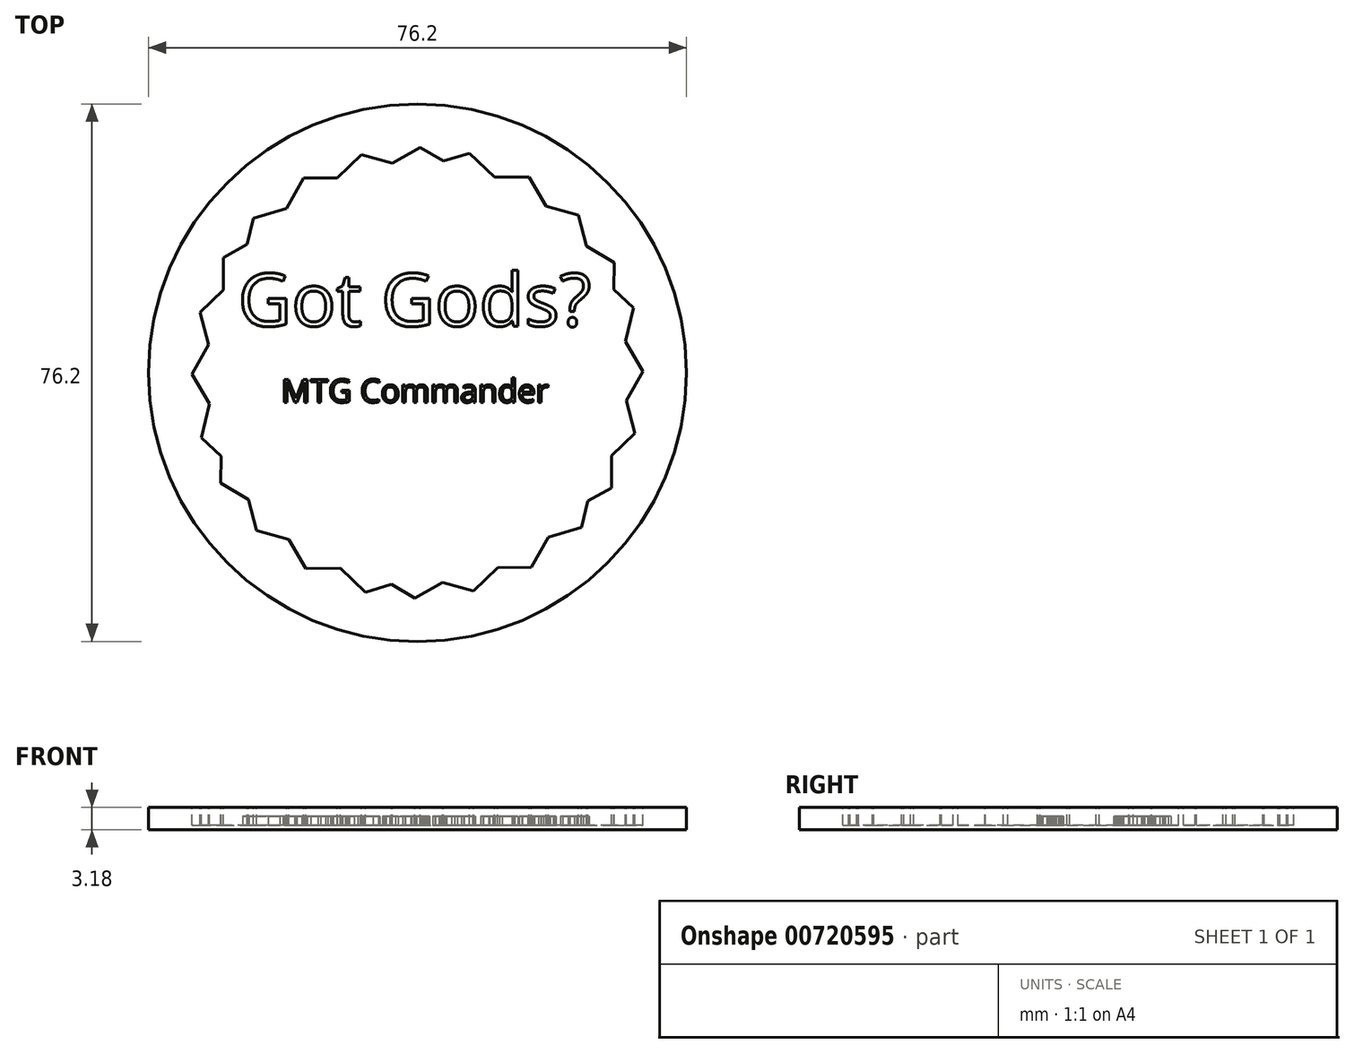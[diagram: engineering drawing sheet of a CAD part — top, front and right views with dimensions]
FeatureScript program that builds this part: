
annotation { "Feature Type Name" : "Feature", "Feature Type Description" : "" }
export const myFeature = defineFeature(function(context is Context, id is Id, definition is map)
    precondition{}
    {
        {
            var Q0;
            Q0=qCreatedBy(makeId("Top.planeOp"),FACE);
            var sketch = newSketch(context, id + "F0", { "sketchPlane" : qUnion([Q0])});
            skCircle(sketch, "E0", {"center": v(0, 0) * mm, "radius": 38.1 * mm});
            skSolve(sketch);
        }
        {
            var Q0;
            Q0=makeQuery(id+"F0.imprint","IMPRINT",FACE,{"disambiguationData":[TD([[makeQuery(id+"F0.imprint","IMPRINT",EDGE,{"derivedFrom":sQuery(id+"F0.wireOp",EDGE,"E0")}),1.0]])]});
            extrude(context, id + "F1", {"entities" : qUnion([Q0]), "depth" : 3.17 * mm, "offsetDistance" : 25.4 * mm});
        }
        {
            var Q0;
            Q0=makeQuery(id+"F1.opExtrude","CAP_FACE",FACE,{"disambiguationData":[OSD([sQuery(id+"F0.wireOp",EDGE,"E0")])],"isStart":false});
            var sketch = newSketch(context, id + "F2", { "sketchPlane" : qUnion([Q0])});
            skCircle(sketch, "E1", {"center": v(0, 0) * mm, "radius": 34.93 * mm});
            skCircle(sketch, "E2.cCircle", {"center": v(0, 0) * mm, "radius": 27.67 * mm, "construction": true});
            skLineSegment(sketch, "E2.0", {"start": v(15.83, 27.75) * mm, "end": v(31.95, 0.17) * mm});
            skLineSegment(sketch, "E2.1", {"start": v(31.95, 0.17) * mm, "end": v(16.12, -27.58) * mm});
            skLineSegment(sketch, "E2.2", {"start": v(16.12, -27.58) * mm, "end": v(-15.83, -27.75) * mm});
            skLineSegment(sketch, "E2.3", {"start": v(-15.83, -27.75) * mm, "end": v(-31.95, -0.17) * mm});
            skLineSegment(sketch, "E2.4", {"start": v(-31.95, -0.17) * mm, "end": v(-16.12, 27.58) * mm});
            skLineSegment(sketch, "E2.5", {"start": v(-16.12, 27.58) * mm, "end": v(15.83, 27.75) * mm});
            skPoint(sketch, "E2.0.midPoint", {"position": v(23.89, 13.96) * mm});
            skLineSegment(sketch, "E3.0", {"start": v(0.4, 31.95) * mm, "end": v(27.87, 15.63) * mm});
            skLineSegment(sketch, "E3.1", {"start": v(27.87, 15.63) * mm, "end": v(27.47, -16.32) * mm});
            skLineSegment(sketch, "E3.2", {"start": v(27.47, -16.32) * mm, "end": v(-0.4, -31.95) * mm});
            skLineSegment(sketch, "E3.3", {"start": v(-0.4, -31.95) * mm, "end": v(-27.87, -15.63) * mm});
            skLineSegment(sketch, "E3.4", {"start": v(-27.87, -15.63) * mm, "end": v(-27.47, 16.32) * mm});
            skLineSegment(sketch, "E3.5", {"start": v(-27.47, 16.32) * mm, "end": v(0.4, 31.95) * mm});
            skPoint(sketch, "E3.0.midPoint", {"position": v(14.13, 23.79) * mm});
            skLineSegment(sketch, "E4.0", {"start": v(22.82, 22.36) * mm, "end": v(30.78, -8.58) * mm});
            skLineSegment(sketch, "E4.1", {"start": v(30.78, -8.58) * mm, "end": v(7.96, -30.94) * mm});
            skLineSegment(sketch, "E4.2", {"start": v(7.96, -30.94) * mm, "end": v(-22.82, -22.36) * mm});
            skLineSegment(sketch, "E4.3", {"start": v(-22.82, -22.36) * mm, "end": v(-30.78, 8.58) * mm});
            skLineSegment(sketch, "E4.4", {"start": v(-30.78, 8.58) * mm, "end": v(-7.96, 30.94) * mm});
            skLineSegment(sketch, "E4.5", {"start": v(-7.96, 30.94) * mm, "end": v(22.82, 22.36) * mm});
            skPoint(sketch, "E4.0.midPoint", {"position": v(26.8, 6.9) * mm});
            skLineSegment(sketch, "E5.0", {"start": v(-23.26, 21.9) * mm, "end": v(7.34, 31.1) * mm});
            skLineSegment(sketch, "E5.1", {"start": v(7.34, 31.1) * mm, "end": v(30.6, 9.19) * mm});
            skLineSegment(sketch, "E5.2", {"start": v(30.6, 9.19) * mm, "end": v(23.26, -21.9) * mm});
            skLineSegment(sketch, "E5.3", {"start": v(23.26, -21.9) * mm, "end": v(-7.34, -31.1) * mm});
            skLineSegment(sketch, "E5.4", {"start": v(-7.34, -31.1) * mm, "end": v(-30.6, -9.19) * mm});
            skLineSegment(sketch, "E5.5", {"start": v(-30.6, -9.19) * mm, "end": v(-23.26, 21.9) * mm});
            skPoint(sketch, "E5.0.midPoint", {"position": v(-7.96, 26.5) * mm});
            skSolve(sketch);
        }
        {
            var Q0;
            {var subQ0=sQuery(id+"F2.wireOp",EDGE,"E4.2");var subQ1=sQuery(id+"F2.wireOp",EDGE,"E2.3");var subQ2=makeQuery(id+"F2.imprint","INTERSECT",VERTEX,{"derivedFrom":[subQ1,subQ0]});Q0=makeQuery(id+"F2.imprint","IMPRINT",FACE,{"disambiguationData":[TD([[makeQuery(id+"F2.imprint","IMPRINT",EDGE,{"disambiguationData":[TD([[subQ2,-1.0]])],"derivedFrom":subQ1}),-1.0]])]});}
            var Q1;
            {var subQ0=sQuery(id+"F2.wireOp",EDGE,"E2.3");var subQ1=sQuery(id+"F2.wireOp",EDGE,"E2.2");var subQ2=makeQuery(id+"F2.imprint","INTERSECT",VERTEX,{"derivedFrom":[subQ1,subQ0]});Q1=makeQuery(id+"F2.imprint","IMPRINT",FACE,{"disambiguationData":[TD([[makeQuery(id+"F2.imprint","IMPRINT",EDGE,{"disambiguationData":[TD([[subQ2,1.0]])],"derivedFrom":subQ1}),-1.0]])]});}
            var Q2;
            {var subQ0=sQuery(id+"F2.wireOp",EDGE,"E4.2");var subQ1=sQuery(id+"F2.wireOp",EDGE,"E2.2");var subQ2=makeQuery(id+"F2.imprint","INTERSECT",VERTEX,{"derivedFrom":[subQ1,subQ0]});Q2=makeQuery(id+"F2.imprint","IMPRINT",FACE,{"disambiguationData":[TD([[makeQuery(id+"F2.imprint","IMPRINT",EDGE,{"disambiguationData":[TD([[subQ2,-1.0]])],"derivedFrom":subQ1}),-1.0]])]});}
            var Q3;
            {var subQ0=sQuery(id+"F2.wireOp",EDGE,"E4.2");var subQ1=sQuery(id+"F2.wireOp",EDGE,"E2.2");var subQ2=makeQuery(id+"F2.imprint","INTERSECT",VERTEX,{"derivedFrom":[subQ1,subQ0]});Q3=makeQuery(id+"F2.imprint","IMPRINT",FACE,{"disambiguationData":[TD([[makeQuery(id+"F2.imprint","IMPRINT",EDGE,{"disambiguationData":[TD([[subQ2,-1.0]])],"derivedFrom":subQ1}),1.0]])]});}
            var Q4;
            {var subQ0=sQuery(id+"F2.wireOp",EDGE,"E3.2");var subQ1=sQuery(id+"F2.wireOp",EDGE,"E2.2");var subQ2=makeQuery(id+"F2.imprint","INTERSECT",VERTEX,{"derivedFrom":[subQ1,subQ0]});Q4=makeQuery(id+"F2.imprint","IMPRINT",FACE,{"disambiguationData":[TD([[makeQuery(id+"F2.imprint","IMPRINT",EDGE,{"disambiguationData":[TD([[subQ2,-1.0]])],"derivedFrom":subQ1}),1.0]])]});}
            var Q5;
            {var subQ0=sQuery(id+"F2.wireOp",EDGE,"E4.1");var subQ1=sQuery(id+"F2.wireOp",EDGE,"E2.2");var subQ2=makeQuery(id+"F2.imprint","INTERSECT",VERTEX,{"derivedFrom":[subQ1,subQ0]});Q5=makeQuery(id+"F2.imprint","IMPRINT",FACE,{"disambiguationData":[TD([[makeQuery(id+"F2.imprint","IMPRINT",EDGE,{"disambiguationData":[TD([[subQ2,-1.0]])],"derivedFrom":subQ1}),1.0]])]});}
            var Q6;
            {var subQ0=sQuery(id+"F2.wireOp",EDGE,"E4.1");var subQ1=sQuery(id+"F2.wireOp",EDGE,"E2.2");var subQ2=makeQuery(id+"F2.imprint","INTERSECT",VERTEX,{"derivedFrom":[subQ1,subQ0]});Q6=makeQuery(id+"F2.imprint","IMPRINT",FACE,{"disambiguationData":[TD([[makeQuery(id+"F2.imprint","IMPRINT",EDGE,{"disambiguationData":[TD([[subQ2,-1.0]])],"derivedFrom":subQ1}),-1.0]])]});}
            var Q7;
            {var subQ0=sQuery(id+"F2.wireOp",EDGE,"E2.2");var subQ1=sQuery(id+"F2.wireOp",EDGE,"E2.1");var subQ2=makeQuery(id+"F2.imprint","INTERSECT",VERTEX,{"derivedFrom":[subQ1,subQ0]});Q7=makeQuery(id+"F2.imprint","IMPRINT",FACE,{"disambiguationData":[TD([[makeQuery(id+"F2.imprint","IMPRINT",EDGE,{"disambiguationData":[TD([[subQ2,1.0]])],"derivedFrom":subQ1}),-1.0]])]});}
            var Q8;
            {var subQ15=sQuery(id+"F2.wireOp",EDGE,"E3.0");var subQ16=sQuery(id+"F2.wireOp",EDGE,"E2.0");var subQ17=makeQuery(id+"F2.imprint","INTERSECT",VERTEX,{"derivedFrom":[subQ16,subQ15]});Q8=makeQuery(id+"F2.imprint","IMPRINT",FACE,{"disambiguationData":[TD([[makeQuery(id+"F2.imprint","IMPRINT",EDGE,{"disambiguationData":[TD([[subQ17,-1.0]])],"derivedFrom":subQ16}),-1.0]])]});}
            var Q9;
            {var subQ0=sQuery(id+"F2.wireOp",EDGE,"E4.1");var subQ1=sQuery(id+"F2.wireOp",EDGE,"E2.1");var subQ2=makeQuery(id+"F2.imprint","INTERSECT",VERTEX,{"derivedFrom":[subQ1,subQ0]});Q9=makeQuery(id+"F2.imprint","IMPRINT",FACE,{"disambiguationData":[TD([[makeQuery(id+"F2.imprint","IMPRINT",EDGE,{"disambiguationData":[TD([[subQ2,-1.0]])],"derivedFrom":subQ1}),-1.0]])]});}
            var Q10;
            {var subQ0=sQuery(id+"F2.wireOp",EDGE,"E4.1");var subQ1=sQuery(id+"F2.wireOp",EDGE,"E2.1");var subQ2=makeQuery(id+"F2.imprint","INTERSECT",VERTEX,{"derivedFrom":[subQ1,subQ0]});Q10=makeQuery(id+"F2.imprint","IMPRINT",FACE,{"disambiguationData":[TD([[makeQuery(id+"F2.imprint","IMPRINT",EDGE,{"disambiguationData":[TD([[subQ2,-1.0]])],"derivedFrom":subQ1}),1.0]])]});}
            var Q11;
            {var subQ0=sQuery(id+"F2.wireOp",EDGE,"E3.1");var subQ1=sQuery(id+"F2.wireOp",EDGE,"E2.1");var subQ2=makeQuery(id+"F2.imprint","INTERSECT",VERTEX,{"derivedFrom":[subQ1,subQ0]});Q11=makeQuery(id+"F2.imprint","IMPRINT",FACE,{"disambiguationData":[TD([[makeQuery(id+"F2.imprint","IMPRINT",EDGE,{"disambiguationData":[TD([[subQ2,-1.0]])],"derivedFrom":subQ1}),1.0]])]});}
            var Q12;
            {var subQ0=sQuery(id+"F2.wireOp",EDGE,"E4.0");var subQ1=sQuery(id+"F2.wireOp",EDGE,"E2.1");var subQ2=makeQuery(id+"F2.imprint","INTERSECT",VERTEX,{"derivedFrom":[subQ1,subQ0]});Q12=makeQuery(id+"F2.imprint","IMPRINT",FACE,{"disambiguationData":[TD([[makeQuery(id+"F2.imprint","IMPRINT",EDGE,{"disambiguationData":[TD([[subQ2,-1.0]])],"derivedFrom":subQ1}),1.0]])]});}
            var Q13;
            {var subQ0=sQuery(id+"F2.wireOp",EDGE,"E4.0");var subQ1=sQuery(id+"F2.wireOp",EDGE,"E2.1");var subQ2=makeQuery(id+"F2.imprint","INTERSECT",VERTEX,{"derivedFrom":[subQ1,subQ0]});Q13=makeQuery(id+"F2.imprint","IMPRINT",FACE,{"disambiguationData":[TD([[makeQuery(id+"F2.imprint","IMPRINT",EDGE,{"disambiguationData":[TD([[subQ2,-1.0]])],"derivedFrom":subQ1}),-1.0]])]});}
            var Q14;
            {var subQ0=sQuery(id+"F2.wireOp",EDGE,"E2.1");var subQ1=sQuery(id+"F2.wireOp",EDGE,"E2.0");var subQ2=makeQuery(id+"F2.imprint","INTERSECT",VERTEX,{"derivedFrom":[subQ1,subQ0]});Q14=makeQuery(id+"F2.imprint","IMPRINT",FACE,{"disambiguationData":[TD([[makeQuery(id+"F2.imprint","IMPRINT",EDGE,{"disambiguationData":[TD([[subQ2,1.0]])],"derivedFrom":subQ1}),-1.0]])]});}
            var Q15;
            {var subQ0=sQuery(id+"F2.wireOp",EDGE,"E4.0");var subQ1=sQuery(id+"F2.wireOp",EDGE,"E2.0");var subQ2=makeQuery(id+"F2.imprint","INTERSECT",VERTEX,{"derivedFrom":[subQ1,subQ0]});Q15=makeQuery(id+"F2.imprint","IMPRINT",FACE,{"disambiguationData":[TD([[makeQuery(id+"F2.imprint","IMPRINT",EDGE,{"disambiguationData":[TD([[subQ2,-1.0]])],"derivedFrom":subQ1}),-1.0]])]});}
            var Q16;
            {var subQ0=sQuery(id+"F2.wireOp",EDGE,"E4.0");var subQ1=sQuery(id+"F2.wireOp",EDGE,"E2.0");var subQ2=makeQuery(id+"F2.imprint","INTERSECT",VERTEX,{"derivedFrom":[subQ1,subQ0]});Q16=makeQuery(id+"F2.imprint","IMPRINT",FACE,{"disambiguationData":[TD([[makeQuery(id+"F2.imprint","IMPRINT",EDGE,{"disambiguationData":[TD([[subQ2,-1.0]])],"derivedFrom":subQ1}),1.0]])]});}
            var Q17;
            {var subQ0=sQuery(id+"F2.wireOp",EDGE,"E3.0");var subQ1=sQuery(id+"F2.wireOp",EDGE,"E2.0");var subQ2=makeQuery(id+"F2.imprint","INTERSECT",VERTEX,{"derivedFrom":[subQ1,subQ0]});Q17=makeQuery(id+"F2.imprint","IMPRINT",FACE,{"disambiguationData":[TD([[makeQuery(id+"F2.imprint","IMPRINT",EDGE,{"disambiguationData":[TD([[subQ2,-1.0]])],"derivedFrom":subQ1}),1.0]])]});}
            var Q18;
            {var subQ0=sQuery(id+"F2.wireOp",EDGE,"E4.5");var subQ1=sQuery(id+"F2.wireOp",EDGE,"E2.0");var subQ2=makeQuery(id+"F2.imprint","INTERSECT",VERTEX,{"derivedFrom":[subQ1,subQ0]});Q18=makeQuery(id+"F2.imprint","IMPRINT",FACE,{"disambiguationData":[TD([[makeQuery(id+"F2.imprint","IMPRINT",EDGE,{"disambiguationData":[TD([[subQ2,-1.0]])],"derivedFrom":subQ1}),1.0]])]});}
            var Q19;
            {var subQ0=sQuery(id+"F2.wireOp",EDGE,"E4.5");var subQ1=sQuery(id+"F2.wireOp",EDGE,"E2.0");var subQ2=makeQuery(id+"F2.imprint","INTERSECT",VERTEX,{"derivedFrom":[subQ1,subQ0]});Q19=makeQuery(id+"F2.imprint","IMPRINT",FACE,{"disambiguationData":[TD([[makeQuery(id+"F2.imprint","IMPRINT",EDGE,{"disambiguationData":[TD([[subQ2,-1.0]])],"derivedFrom":subQ1}),-1.0]])]});}
            var Q20;
            {var subQ0=sQuery(id+"F2.wireOp",EDGE,"E2.5");var subQ1=sQuery(id+"F2.wireOp",EDGE,"E2.0");var subQ2=makeQuery(id+"F2.imprint","INTERSECT",VERTEX,{"derivedFrom":[subQ1,subQ0]});Q20=makeQuery(id+"F2.imprint","IMPRINT",FACE,{"disambiguationData":[TD([[makeQuery(id+"F2.imprint","IMPRINT",EDGE,{"disambiguationData":[TD([[subQ2,-1.0]])],"derivedFrom":subQ1}),-1.0]])]});}
            var Q21;
            {var subQ0=sQuery(id+"F2.wireOp",EDGE,"E4.5");var subQ1=sQuery(id+"F2.wireOp",EDGE,"E2.5");var subQ2=makeQuery(id+"F2.imprint","INTERSECT",VERTEX,{"derivedFrom":[subQ1,subQ0]});Q21=makeQuery(id+"F2.imprint","IMPRINT",FACE,{"disambiguationData":[TD([[makeQuery(id+"F2.imprint","IMPRINT",EDGE,{"disambiguationData":[TD([[subQ2,-1.0]])],"derivedFrom":subQ1}),1.0]])]});}
            var Q22;
            {var subQ0=sQuery(id+"F2.wireOp",EDGE,"E3.5");var subQ1=sQuery(id+"F2.wireOp",EDGE,"E2.5");var subQ2=makeQuery(id+"F2.imprint","INTERSECT",VERTEX,{"derivedFrom":[subQ1,subQ0]});Q22=makeQuery(id+"F2.imprint","IMPRINT",FACE,{"disambiguationData":[TD([[makeQuery(id+"F2.imprint","IMPRINT",EDGE,{"disambiguationData":[TD([[subQ2,-1.0]])],"derivedFrom":subQ1}),1.0]])]});}
            var Q23;
            {var subQ0=sQuery(id+"F2.wireOp",EDGE,"E4.5");var subQ1=sQuery(id+"F2.wireOp",EDGE,"E2.5");var subQ2=makeQuery(id+"F2.imprint","INTERSECT",VERTEX,{"derivedFrom":[subQ1,subQ0]});Q23=makeQuery(id+"F2.imprint","IMPRINT",FACE,{"disambiguationData":[TD([[makeQuery(id+"F2.imprint","IMPRINT",EDGE,{"disambiguationData":[TD([[subQ2,-1.0]])],"derivedFrom":subQ1}),-1.0]])]});}
            var Q24;
            {var subQ0=sQuery(id+"F2.wireOp",EDGE,"E4.4");var subQ1=sQuery(id+"F2.wireOp",EDGE,"E2.5");var subQ2=makeQuery(id+"F2.imprint","INTERSECT",VERTEX,{"derivedFrom":[subQ1,subQ0]});Q24=makeQuery(id+"F2.imprint","IMPRINT",FACE,{"disambiguationData":[TD([[makeQuery(id+"F2.imprint","IMPRINT",EDGE,{"disambiguationData":[TD([[subQ2,-1.0]])],"derivedFrom":subQ1}),-1.0]])]});}
            var Q25;
            {var subQ0=sQuery(id+"F2.wireOp",EDGE,"E4.4");var subQ1=sQuery(id+"F2.wireOp",EDGE,"E2.5");var subQ2=makeQuery(id+"F2.imprint","INTERSECT",VERTEX,{"derivedFrom":[subQ1,subQ0]});Q25=makeQuery(id+"F2.imprint","IMPRINT",FACE,{"disambiguationData":[TD([[makeQuery(id+"F2.imprint","IMPRINT",EDGE,{"disambiguationData":[TD([[subQ2,-1.0]])],"derivedFrom":subQ1}),1.0]])]});}
            var Q26;
            {var subQ0=sQuery(id+"F2.wireOp",EDGE,"E2.5");var subQ1=sQuery(id+"F2.wireOp",EDGE,"E2.4");var subQ2=makeQuery(id+"F2.imprint","INTERSECT",VERTEX,{"derivedFrom":[subQ1,subQ0]});Q26=makeQuery(id+"F2.imprint","IMPRINT",FACE,{"disambiguationData":[TD([[makeQuery(id+"F2.imprint","IMPRINT",EDGE,{"disambiguationData":[TD([[subQ2,1.0]])],"derivedFrom":subQ1}),-1.0]])]});}
            var Q27;
            {var subQ0=sQuery(id+"F2.wireOp",EDGE,"E4.4");var subQ1=sQuery(id+"F2.wireOp",EDGE,"E2.4");var subQ2=makeQuery(id+"F2.imprint","INTERSECT",VERTEX,{"derivedFrom":[subQ1,subQ0]});Q27=makeQuery(id+"F2.imprint","IMPRINT",FACE,{"disambiguationData":[TD([[makeQuery(id+"F2.imprint","IMPRINT",EDGE,{"disambiguationData":[TD([[subQ2,-1.0]])],"derivedFrom":subQ1}),-1.0]])]});}
            var Q28;
            {var subQ0=sQuery(id+"F2.wireOp",EDGE,"E4.4");var subQ1=sQuery(id+"F2.wireOp",EDGE,"E2.4");var subQ2=makeQuery(id+"F2.imprint","INTERSECT",VERTEX,{"derivedFrom":[subQ1,subQ0]});Q28=makeQuery(id+"F2.imprint","IMPRINT",FACE,{"disambiguationData":[TD([[makeQuery(id+"F2.imprint","IMPRINT",EDGE,{"disambiguationData":[TD([[subQ2,-1.0]])],"derivedFrom":subQ1}),1.0]])]});}
            var Q29;
            {var subQ0=sQuery(id+"F2.wireOp",EDGE,"E3.4");var subQ1=sQuery(id+"F2.wireOp",EDGE,"E2.4");var subQ2=makeQuery(id+"F2.imprint","INTERSECT",VERTEX,{"derivedFrom":[subQ1,subQ0]});Q29=makeQuery(id+"F2.imprint","IMPRINT",FACE,{"disambiguationData":[TD([[makeQuery(id+"F2.imprint","IMPRINT",EDGE,{"disambiguationData":[TD([[subQ2,-1.0]])],"derivedFrom":subQ1}),1.0]])]});}
            var Q30;
            {var subQ0=sQuery(id+"F2.wireOp",EDGE,"E4.3");var subQ1=sQuery(id+"F2.wireOp",EDGE,"E2.4");var subQ2=makeQuery(id+"F2.imprint","INTERSECT",VERTEX,{"derivedFrom":[subQ1,subQ0]});Q30=makeQuery(id+"F2.imprint","IMPRINT",FACE,{"disambiguationData":[TD([[makeQuery(id+"F2.imprint","IMPRINT",EDGE,{"disambiguationData":[TD([[subQ2,-1.0]])],"derivedFrom":subQ1}),1.0]])]});}
            var Q31;
            {var subQ0=sQuery(id+"F2.wireOp",EDGE,"E4.3");var subQ1=sQuery(id+"F2.wireOp",EDGE,"E2.4");var subQ2=makeQuery(id+"F2.imprint","INTERSECT",VERTEX,{"derivedFrom":[subQ1,subQ0]});Q31=makeQuery(id+"F2.imprint","IMPRINT",FACE,{"disambiguationData":[TD([[makeQuery(id+"F2.imprint","IMPRINT",EDGE,{"disambiguationData":[TD([[subQ2,-1.0]])],"derivedFrom":subQ1}),-1.0]])]});}
            var Q32;
            {var subQ0=sQuery(id+"F2.wireOp",EDGE,"E2.4");var subQ1=sQuery(id+"F2.wireOp",EDGE,"E2.3");var subQ2=makeQuery(id+"F2.imprint","INTERSECT",VERTEX,{"derivedFrom":[subQ1,subQ0]});Q32=makeQuery(id+"F2.imprint","IMPRINT",FACE,{"disambiguationData":[TD([[makeQuery(id+"F2.imprint","IMPRINT",EDGE,{"disambiguationData":[TD([[subQ2,1.0]])],"derivedFrom":subQ1}),-1.0]])]});}
            var Q33;
            {var subQ0=sQuery(id+"F2.wireOp",EDGE,"E4.3");var subQ1=sQuery(id+"F2.wireOp",EDGE,"E2.3");var subQ2=makeQuery(id+"F2.imprint","INTERSECT",VERTEX,{"derivedFrom":[subQ1,subQ0]});Q33=makeQuery(id+"F2.imprint","IMPRINT",FACE,{"disambiguationData":[TD([[makeQuery(id+"F2.imprint","IMPRINT",EDGE,{"disambiguationData":[TD([[subQ2,-1.0]])],"derivedFrom":subQ1}),-1.0]])]});}
            var Q34;
            {var subQ0=sQuery(id+"F2.wireOp",EDGE,"E3.3");var subQ1=sQuery(id+"F2.wireOp",EDGE,"E2.3");var subQ2=makeQuery(id+"F2.imprint","INTERSECT",VERTEX,{"derivedFrom":[subQ1,subQ0]});Q34=makeQuery(id+"F2.imprint","IMPRINT",FACE,{"disambiguationData":[TD([[makeQuery(id+"F2.imprint","IMPRINT",EDGE,{"disambiguationData":[TD([[subQ2,-1.0]])],"derivedFrom":subQ1}),1.0]])]});}
            var Q35;
            {var subQ0=sQuery(id+"F2.wireOp",EDGE,"E4.3");var subQ1=sQuery(id+"F2.wireOp",EDGE,"E2.3");var subQ2=makeQuery(id+"F2.imprint","INTERSECT",VERTEX,{"derivedFrom":[subQ1,subQ0]});Q35=makeQuery(id+"F2.imprint","IMPRINT",FACE,{"disambiguationData":[TD([[makeQuery(id+"F2.imprint","IMPRINT",EDGE,{"disambiguationData":[TD([[subQ2,-1.0]])],"derivedFrom":subQ1}),1.0]])]});}
            var Q36;
            {var subQ0=sQuery(id+"F2.wireOp",EDGE,"E3.4");var subQ1=sQuery(id+"F2.wireOp",EDGE,"E3.3");var subQ2=makeQuery(id+"F2.imprint","INTERSECT",VERTEX,{"derivedFrom":[subQ1,subQ0]});Q36=makeQuery(id+"F2.imprint","IMPRINT",FACE,{"disambiguationData":[TD([[makeQuery(id+"F2.imprint","IMPRINT",EDGE,{"disambiguationData":[TD([[subQ2,1.0]])],"derivedFrom":subQ1}),-1.0]])]});}
            var Q37;
            {var subQ0=sQuery(id+"F2.wireOp",EDGE,"E3.4");var subQ1=sQuery(id+"F2.wireOp",EDGE,"E2.3");var subQ2=makeQuery(id+"F2.imprint","INTERSECT",VERTEX,{"derivedFrom":[subQ1,subQ0]});Q37=makeQuery(id+"F2.imprint","IMPRINT",FACE,{"disambiguationData":[TD([[makeQuery(id+"F2.imprint","IMPRINT",EDGE,{"disambiguationData":[TD([[subQ2,-1.0]])],"derivedFrom":subQ1}),1.0]])]});}
            var Q38;
            {var subQ0=sQuery(id+"F2.wireOp",EDGE,"E3.4");var subQ1=sQuery(id+"F2.wireOp",EDGE,"E2.3");var subQ2=makeQuery(id+"F2.imprint","INTERSECT",VERTEX,{"derivedFrom":[subQ1,subQ0]});Q38=makeQuery(id+"F2.imprint","IMPRINT",FACE,{"disambiguationData":[TD([[makeQuery(id+"F2.imprint","IMPRINT",EDGE,{"disambiguationData":[TD([[subQ2,-1.0]])],"derivedFrom":subQ1}),-1.0]])]});}
            var Q39;
            {var subQ0=sQuery(id+"F2.wireOp",EDGE,"E4.3");var subQ1=sQuery(id+"F2.wireOp",EDGE,"E3.4");var subQ2=makeQuery(id+"F2.imprint","INTERSECT",VERTEX,{"derivedFrom":[subQ1,subQ0]});Q39=makeQuery(id+"F2.imprint","IMPRINT",FACE,{"disambiguationData":[TD([[makeQuery(id+"F2.imprint","IMPRINT",EDGE,{"disambiguationData":[TD([[subQ2,-1.0]])],"derivedFrom":subQ1}),1.0]])]});}
            var Q40;
            {var subQ0=sQuery(id+"F2.wireOp",EDGE,"E3.4");var subQ1=sQuery(id+"F2.wireOp",EDGE,"E2.4");var subQ2=makeQuery(id+"F2.imprint","INTERSECT",VERTEX,{"derivedFrom":[subQ1,subQ0]});Q40=makeQuery(id+"F2.imprint","IMPRINT",FACE,{"disambiguationData":[TD([[makeQuery(id+"F2.imprint","IMPRINT",EDGE,{"disambiguationData":[TD([[subQ2,-1.0]])],"derivedFrom":subQ1}),-1.0]])]});}
            var Q41;
            {var subQ0=sQuery(id+"F2.wireOp",EDGE,"E5.5");var subQ1=sQuery(id+"F2.wireOp",EDGE,"E2.4");var subQ2=makeQuery(id+"F2.imprint","INTERSECT",VERTEX,{"derivedFrom":[subQ1,subQ0]});Q41=makeQuery(id+"F2.imprint","IMPRINT",FACE,{"disambiguationData":[TD([[makeQuery(id+"F2.imprint","IMPRINT",EDGE,{"disambiguationData":[TD([[subQ2,-1.0]])],"derivedFrom":subQ1}),1.0]])]});}
            var Q42;
            {var subQ0=sQuery(id+"F2.wireOp",EDGE,"E3.5");var subQ1=sQuery(id+"F2.wireOp",EDGE,"E3.4");var subQ2=makeQuery(id+"F2.imprint","INTERSECT",VERTEX,{"derivedFrom":[subQ1,subQ0]});Q42=makeQuery(id+"F2.imprint","IMPRINT",FACE,{"disambiguationData":[TD([[makeQuery(id+"F2.imprint","IMPRINT",EDGE,{"disambiguationData":[TD([[subQ2,1.0]])],"derivedFrom":subQ1}),-1.0]])]});}
            var Q43;
            {var subQ0=sQuery(id+"F2.wireOp",EDGE,"E3.5");var subQ1=sQuery(id+"F2.wireOp",EDGE,"E2.4");var subQ2=makeQuery(id+"F2.imprint","INTERSECT",VERTEX,{"derivedFrom":[subQ1,subQ0]});Q43=makeQuery(id+"F2.imprint","IMPRINT",FACE,{"disambiguationData":[TD([[makeQuery(id+"F2.imprint","IMPRINT",EDGE,{"disambiguationData":[TD([[subQ2,-1.0]])],"derivedFrom":subQ1}),1.0]])]});}
            var Q44;
            {var subQ0=sQuery(id+"F2.wireOp",EDGE,"E3.0");var subQ1=sQuery(id+"F2.wireOp",EDGE,"E2.5");var subQ2=makeQuery(id+"F2.imprint","INTERSECT",VERTEX,{"derivedFrom":[subQ1,subQ0]});Q44=makeQuery(id+"F2.imprint","IMPRINT",FACE,{"disambiguationData":[TD([[makeQuery(id+"F2.imprint","IMPRINT",EDGE,{"disambiguationData":[TD([[subQ2,-1.0]])],"derivedFrom":subQ1}),1.0]])]});}
            var Q45;
            {var subQ0=sQuery(id+"F2.wireOp",EDGE,"E3.5");var subQ1=sQuery(id+"F2.wireOp",EDGE,"E3.0");var subQ2=makeQuery(id+"F2.imprint","INTERSECT",VERTEX,{"derivedFrom":[subQ1,subQ0]});Q45=makeQuery(id+"F2.imprint","IMPRINT",FACE,{"disambiguationData":[TD([[makeQuery(id+"F2.imprint","IMPRINT",EDGE,{"disambiguationData":[TD([[subQ2,-1.0]])],"derivedFrom":subQ1}),-1.0]])]});}
            var Q46;
            {var subQ0=sQuery(id+"F2.wireOp",EDGE,"E5.0");var subQ1=sQuery(id+"F2.wireOp",EDGE,"E2.5");var subQ2=makeQuery(id+"F2.imprint","INTERSECT",VERTEX,{"derivedFrom":[subQ1,subQ0]});Q46=makeQuery(id+"F2.imprint","IMPRINT",FACE,{"disambiguationData":[TD([[makeQuery(id+"F2.imprint","IMPRINT",EDGE,{"disambiguationData":[TD([[subQ2,-1.0]])],"derivedFrom":subQ1}),1.0]])]});}
            var Q47;
            {var subQ0=sQuery(id+"F2.wireOp",EDGE,"E3.5");var subQ1=sQuery(id+"F2.wireOp",EDGE,"E2.5");var subQ2=makeQuery(id+"F2.imprint","INTERSECT",VERTEX,{"derivedFrom":[subQ1,subQ0]});Q47=makeQuery(id+"F2.imprint","IMPRINT",FACE,{"disambiguationData":[TD([[makeQuery(id+"F2.imprint","IMPRINT",EDGE,{"disambiguationData":[TD([[subQ2,-1.0]])],"derivedFrom":subQ1}),-1.0]])]});}
            var Q48;
            {var subQ0=sQuery(id+"F2.wireOp",EDGE,"E3.5");var subQ1=sQuery(id+"F2.wireOp",EDGE,"E2.4");var subQ2=makeQuery(id+"F2.imprint","INTERSECT",VERTEX,{"derivedFrom":[subQ1,subQ0]});Q48=makeQuery(id+"F2.imprint","IMPRINT",FACE,{"disambiguationData":[TD([[makeQuery(id+"F2.imprint","IMPRINT",EDGE,{"disambiguationData":[TD([[subQ2,-1.0]])],"derivedFrom":subQ1}),-1.0]])]});}
            var Q49;
            {var subQ0=sQuery(id+"F2.wireOp",EDGE,"E3.1");var subQ1=sQuery(id+"F2.wireOp",EDGE,"E2.0");var subQ2=makeQuery(id+"F2.imprint","INTERSECT",VERTEX,{"derivedFrom":[subQ1,subQ0]});Q49=makeQuery(id+"F2.imprint","IMPRINT",FACE,{"disambiguationData":[TD([[makeQuery(id+"F2.imprint","IMPRINT",EDGE,{"disambiguationData":[TD([[subQ2,-1.0]])],"derivedFrom":subQ1}),1.0]])]});}
            var Q50;
            {var subQ0=sQuery(id+"F2.wireOp",EDGE,"E3.1");var subQ1=sQuery(id+"F2.wireOp",EDGE,"E3.0");var subQ2=makeQuery(id+"F2.imprint","INTERSECT",VERTEX,{"derivedFrom":[subQ1,subQ0]});Q50=makeQuery(id+"F2.imprint","IMPRINT",FACE,{"disambiguationData":[TD([[makeQuery(id+"F2.imprint","IMPRINT",EDGE,{"disambiguationData":[TD([[subQ2,1.0]])],"derivedFrom":subQ1}),-1.0]])]});}
            var Q51;
            {var subQ0=sQuery(id+"F2.wireOp",EDGE,"E3.1");var subQ1=sQuery(id+"F2.wireOp",EDGE,"E2.0");var subQ2=makeQuery(id+"F2.imprint","INTERSECT",VERTEX,{"derivedFrom":[subQ1,subQ0]});Q51=makeQuery(id+"F2.imprint","IMPRINT",FACE,{"disambiguationData":[TD([[makeQuery(id+"F2.imprint","IMPRINT",EDGE,{"disambiguationData":[TD([[subQ2,-1.0]])],"derivedFrom":subQ1}),-1.0]])]});}
            var Q52;
            {var subQ0=sQuery(id+"F2.wireOp",EDGE,"E3.2");var subQ1=sQuery(id+"F2.wireOp",EDGE,"E3.1");var subQ2=makeQuery(id+"F2.imprint","INTERSECT",VERTEX,{"derivedFrom":[subQ1,subQ0]});Q52=makeQuery(id+"F2.imprint","IMPRINT",FACE,{"disambiguationData":[TD([[makeQuery(id+"F2.imprint","IMPRINT",EDGE,{"disambiguationData":[TD([[subQ2,1.0]])],"derivedFrom":subQ1}),-1.0]])]});}
            var Q53;
            {var subQ0=sQuery(id+"F2.wireOp",EDGE,"E3.2");var subQ1=sQuery(id+"F2.wireOp",EDGE,"E2.1");var subQ2=makeQuery(id+"F2.imprint","INTERSECT",VERTEX,{"derivedFrom":[subQ1,subQ0]});Q53=makeQuery(id+"F2.imprint","IMPRINT",FACE,{"disambiguationData":[TD([[makeQuery(id+"F2.imprint","IMPRINT",EDGE,{"disambiguationData":[TD([[subQ2,-1.0]])],"derivedFrom":subQ1}),1.0]])]});}
            var Q54;
            {var subQ0=sQuery(id+"F2.wireOp",EDGE,"E3.2");var subQ1=sQuery(id+"F2.wireOp",EDGE,"E2.1");var subQ2=makeQuery(id+"F2.imprint","INTERSECT",VERTEX,{"derivedFrom":[subQ1,subQ0]});Q54=makeQuery(id+"F2.imprint","IMPRINT",FACE,{"disambiguationData":[TD([[makeQuery(id+"F2.imprint","IMPRINT",EDGE,{"disambiguationData":[TD([[subQ2,-1.0]])],"derivedFrom":subQ1}),-1.0]])]});}
            var Q55;
            {var subQ0=sQuery(id+"F2.wireOp",EDGE,"E3.3");var subQ1=sQuery(id+"F2.wireOp",EDGE,"E3.2");var subQ2=makeQuery(id+"F2.imprint","INTERSECT",VERTEX,{"derivedFrom":[subQ1,subQ0]});Q55=makeQuery(id+"F2.imprint","IMPRINT",FACE,{"disambiguationData":[TD([[makeQuery(id+"F2.imprint","IMPRINT",EDGE,{"disambiguationData":[TD([[subQ2,1.0]])],"derivedFrom":subQ1}),-1.0]])]});}
            var Q56;
            {var subQ0=sQuery(id+"F2.wireOp",EDGE,"E3.3");var subQ1=sQuery(id+"F2.wireOp",EDGE,"E2.2");var subQ2=makeQuery(id+"F2.imprint","INTERSECT",VERTEX,{"derivedFrom":[subQ1,subQ0]});Q56=makeQuery(id+"F2.imprint","IMPRINT",FACE,{"disambiguationData":[TD([[makeQuery(id+"F2.imprint","IMPRINT",EDGE,{"disambiguationData":[TD([[subQ2,-1.0]])],"derivedFrom":subQ1}),1.0]])]});}
            var Q57;
            {var subQ0=sQuery(id+"F2.wireOp",EDGE,"E3.3");var subQ1=sQuery(id+"F2.wireOp",EDGE,"E2.2");var subQ2=makeQuery(id+"F2.imprint","INTERSECT",VERTEX,{"derivedFrom":[subQ1,subQ0]});Q57=makeQuery(id+"F2.imprint","IMPRINT",FACE,{"disambiguationData":[TD([[makeQuery(id+"F2.imprint","IMPRINT",EDGE,{"disambiguationData":[TD([[subQ2,-1.0]])],"derivedFrom":subQ1}),-1.0]])]});}
            var Q58;
            {var subQ0=sQuery(id+"F2.wireOp",EDGE,"E3.0");var subQ1=sQuery(id+"F2.wireOp",EDGE,"E2.5");var subQ2=makeQuery(id+"F2.imprint","INTERSECT",VERTEX,{"derivedFrom":[subQ1,subQ0]});Q58=makeQuery(id+"F2.imprint","IMPRINT",FACE,{"disambiguationData":[TD([[makeQuery(id+"F2.imprint","IMPRINT",EDGE,{"disambiguationData":[TD([[subQ2,-1.0]])],"derivedFrom":subQ1}),-1.0]])]});}
            var Q59;
            {var subQ10=sQuery(id+"F2.wireOp",EDGE,"E5.1");var subQ11=sQuery(id+"F2.wireOp",EDGE,"E2.0");var subQ12=makeQuery(id+"F2.imprint","INTERSECT",VERTEX,{"derivedFrom":[subQ11,subQ10]});Q59=makeQuery(id+"F2.imprint","IMPRINT",FACE,{"disambiguationData":[TD([[makeQuery(id+"F2.imprint","IMPRINT",EDGE,{"disambiguationData":[TD([[subQ12,-1.0]])],"derivedFrom":subQ11}),-1.0]])]});}
            var Q60;
            {var subQ0=sQuery(id+"F2.wireOp",EDGE,"E3.1");var subQ1=sQuery(id+"F2.wireOp",EDGE,"E2.1");var subQ2=makeQuery(id+"F2.imprint","INTERSECT",VERTEX,{"derivedFrom":[subQ1,subQ0]});Q60=makeQuery(id+"F2.imprint","IMPRINT",FACE,{"disambiguationData":[TD([[makeQuery(id+"F2.imprint","IMPRINT",EDGE,{"disambiguationData":[TD([[subQ2,-1.0]])],"derivedFrom":subQ1}),-1.0]])]});}
            var Q61;
            {var subQ0=sQuery(id+"F2.wireOp",EDGE,"E5.2");var subQ1=sQuery(id+"F2.wireOp",EDGE,"E2.1");var subQ2=makeQuery(id+"F2.imprint","INTERSECT",VERTEX,{"derivedFrom":[subQ1,subQ0]});Q61=makeQuery(id+"F2.imprint","IMPRINT",FACE,{"disambiguationData":[TD([[makeQuery(id+"F2.imprint","IMPRINT",EDGE,{"disambiguationData":[TD([[subQ2,-1.0]])],"derivedFrom":subQ1}),1.0]])]});}
            var Q62;
            {var subQ0=sQuery(id+"F2.wireOp",EDGE,"E3.2");var subQ1=sQuery(id+"F2.wireOp",EDGE,"E2.2");var subQ2=makeQuery(id+"F2.imprint","INTERSECT",VERTEX,{"derivedFrom":[subQ1,subQ0]});Q62=makeQuery(id+"F2.imprint","IMPRINT",FACE,{"disambiguationData":[TD([[makeQuery(id+"F2.imprint","IMPRINT",EDGE,{"disambiguationData":[TD([[subQ2,-1.0]])],"derivedFrom":subQ1}),-1.0]])]});}
            var Q63;
            {var subQ0=sQuery(id+"F2.wireOp",EDGE,"E4.1");var subQ1=sQuery(id+"F2.wireOp",EDGE,"E3.2");var subQ2=makeQuery(id+"F2.imprint","INTERSECT",VERTEX,{"derivedFrom":[subQ1,subQ0]});Q63=makeQuery(id+"F2.imprint","IMPRINT",FACE,{"disambiguationData":[TD([[makeQuery(id+"F2.imprint","IMPRINT",EDGE,{"disambiguationData":[TD([[subQ2,-1.0]])],"derivedFrom":subQ1}),1.0]])]});}
            var Q64;
            {var subQ0=sQuery(id+"F2.wireOp",EDGE,"E5.3");var subQ1=sQuery(id+"F2.wireOp",EDGE,"E2.2");var subQ2=makeQuery(id+"F2.imprint","INTERSECT",VERTEX,{"derivedFrom":[subQ1,subQ0]});Q64=makeQuery(id+"F2.imprint","IMPRINT",FACE,{"disambiguationData":[TD([[makeQuery(id+"F2.imprint","IMPRINT",EDGE,{"disambiguationData":[TD([[subQ2,-1.0]])],"derivedFrom":subQ1}),1.0]])]});}
            var Q65;
            {var subQ0=sQuery(id+"F2.wireOp",EDGE,"E4.2");var subQ1=sQuery(id+"F2.wireOp",EDGE,"E3.3");var subQ2=makeQuery(id+"F2.imprint","INTERSECT",VERTEX,{"derivedFrom":[subQ1,subQ0]});Q65=makeQuery(id+"F2.imprint","IMPRINT",FACE,{"disambiguationData":[TD([[makeQuery(id+"F2.imprint","IMPRINT",EDGE,{"disambiguationData":[TD([[subQ2,-1.0]])],"derivedFrom":subQ1}),1.0]])]});}
            var Q66;
            {var subQ0=sQuery(id+"F2.wireOp",EDGE,"E4.2");var subQ1=sQuery(id+"F2.wireOp",EDGE,"E2.3");var subQ2=makeQuery(id+"F2.imprint","INTERSECT",VERTEX,{"derivedFrom":[subQ1,subQ0]});Q66=makeQuery(id+"F2.imprint","IMPRINT",FACE,{"disambiguationData":[TD([[makeQuery(id+"F2.imprint","IMPRINT",EDGE,{"disambiguationData":[TD([[subQ2,-1.0]])],"derivedFrom":subQ1}),1.0]])]});}
            var Q67;
            {var subQ0=sQuery(id+"F2.wireOp",EDGE,"E5.4");var subQ1=sQuery(id+"F2.wireOp",EDGE,"E2.3");var subQ2=makeQuery(id+"F2.imprint","INTERSECT",VERTEX,{"derivedFrom":[subQ1,subQ0]});Q67=makeQuery(id+"F2.imprint","IMPRINT",FACE,{"disambiguationData":[TD([[makeQuery(id+"F2.imprint","IMPRINT",EDGE,{"disambiguationData":[TD([[subQ2,-1.0]])],"derivedFrom":subQ1}),1.0]])]});}
            var Q68;
            {var subQ0=sQuery(id+"F2.wireOp",EDGE,"E3.3");var subQ1=sQuery(id+"F2.wireOp",EDGE,"E2.3");var subQ2=makeQuery(id+"F2.imprint","INTERSECT",VERTEX,{"derivedFrom":[subQ1,subQ0]});Q68=makeQuery(id+"F2.imprint","IMPRINT",FACE,{"disambiguationData":[TD([[makeQuery(id+"F2.imprint","IMPRINT",EDGE,{"disambiguationData":[TD([[subQ2,-1.0]])],"derivedFrom":subQ1}),-1.0]])]});}
            var Q69;
            {var subQ0=sQuery(id+"F2.wireOp",EDGE,"E4.5");var subQ1=sQuery(id+"F2.wireOp",EDGE,"E3.0");var subQ2=makeQuery(id+"F2.imprint","INTERSECT",VERTEX,{"derivedFrom":[subQ1,subQ0]});Q69=makeQuery(id+"F2.imprint","IMPRINT",FACE,{"disambiguationData":[TD([[makeQuery(id+"F2.imprint","IMPRINT",EDGE,{"disambiguationData":[TD([[subQ2,-1.0]])],"derivedFrom":subQ1}),1.0]])]});}
            var Q70;
            {var subQ0=sQuery(id+"F2.wireOp",EDGE,"E4.4");var subQ1=sQuery(id+"F2.wireOp",EDGE,"E3.5");var subQ2=makeQuery(id+"F2.imprint","INTERSECT",VERTEX,{"derivedFrom":[subQ1,subQ0]});Q70=makeQuery(id+"F2.imprint","IMPRINT",FACE,{"disambiguationData":[TD([[makeQuery(id+"F2.imprint","IMPRINT",EDGE,{"disambiguationData":[TD([[subQ2,-1.0]])],"derivedFrom":subQ1}),1.0]])]});}
            var Q71;
            {var subQ0=sQuery(id+"F2.wireOp",EDGE,"E5.1");var subQ1=sQuery(id+"F2.wireOp",EDGE,"E2.0");var subQ2=makeQuery(id+"F2.imprint","INTERSECT",VERTEX,{"derivedFrom":[subQ1,subQ0]});Q71=makeQuery(id+"F2.imprint","IMPRINT",FACE,{"disambiguationData":[TD([[makeQuery(id+"F2.imprint","IMPRINT",EDGE,{"disambiguationData":[TD([[subQ2,-1.0]])],"derivedFrom":subQ1}),1.0]])]});}
            var Q72;
            {var subQ0=sQuery(id+"F2.wireOp",EDGE,"E4.0");var subQ1=sQuery(id+"F2.wireOp",EDGE,"E3.1");var subQ2=makeQuery(id+"F2.imprint","INTERSECT",VERTEX,{"derivedFrom":[subQ1,subQ0]});Q72=makeQuery(id+"F2.imprint","IMPRINT",FACE,{"disambiguationData":[TD([[makeQuery(id+"F2.imprint","IMPRINT",EDGE,{"disambiguationData":[TD([[subQ2,-1.0]])],"derivedFrom":subQ1}),1.0]])]});}
            extrude(context, id + "F3", {"entities" : qUnion([Q0, Q1, Q2, Q3, Q4, Q5, Q6, Q7, Q8, Q9, Q10, Q11, Q12, Q13, Q14, Q15, Q16, Q17, Q18, Q19, Q20, Q21, Q22, Q23, Q24, Q25, Q26, Q27, Q28, Q29, Q30, Q31, Q32, Q33, Q34, Q35, Q36, Q37, Q38, Q39, Q40, Q41, Q42, Q43, Q44, Q45, Q46, Q47, Q48, Q49, Q50, Q51, Q52, Q53, Q54, Q55, Q56, Q57, Q58, Q59, Q60, Q61, Q62, Q63, Q64, Q65, Q66, Q67, Q68, Q69, Q70, Q71, Q72]), "operationType" : NewBodyOperationType.REMOVE, "oppositeDirection" : true, "depth" : 2.54 * mm, "offsetDistance" : 25.4 * mm});
        }
        {
            var Q0;
            Q0=makeQuery(id+"F3.boolean.opBoolean","COPY",FACE,{"derivedFrom":makeQuery(id+"F3.opExtrude","CAP_FACE",FACE,{"disambiguationData":[OSD([sQuery(id+"F2.wireOp",EDGE,"E2.0"),sQuery(id+"F2.wireOp",EDGE,"E2.1"),sQuery(id+"F2.wireOp",EDGE,"E2.2"),sQuery(id+"F2.wireOp",EDGE,"E2.3"),sQuery(id+"F2.wireOp",EDGE,"E2.4"),sQuery(id+"F2.wireOp",EDGE,"E2.5"),sQuery(id+"F2.wireOp",EDGE,"E3.0"),sQuery(id+"F2.wireOp",EDGE,"E3.1"),sQuery(id+"F2.wireOp",EDGE,"E3.2"),sQuery(id+"F2.wireOp",EDGE,"E3.3"),sQuery(id+"F2.wireOp",EDGE,"E3.4"),sQuery(id+"F2.wireOp",EDGE,"E3.5"),sQuery(id+"F2.wireOp",EDGE,"E4.0"),sQuery(id+"F2.wireOp",EDGE,"E4.1"),sQuery(id+"F2.wireOp",EDGE,"E4.2"),sQuery(id+"F2.wireOp",EDGE,"E4.3"),sQuery(id+"F2.wireOp",EDGE,"E4.4"),sQuery(id+"F2.wireOp",EDGE,"E4.5")])],"isStart":false})});
            var sketch = newSketch(context, id + "F4", { "sketchPlane" : qUnion([Q0])});
            skText(sketch, "E6", { "text": "MTG Commander\n", "fontName": "OpenSans-Regular.ttf"});
            skText(sketch, "E7", { "text": "Got Gods?\n", "fontName": "OpenSans-Regular.ttf"});
            const initialGuessF4  = {"E6": [-0.01928, -0.0042, 1, 0, 0.00329], "E7": [-0.02543, 0.00661, 1, 0, 0.00751]};
            skSetInitialGuess(sketch, initialGuessF4);
            skSolve(sketch);
        }
        {
            var Q0;
            Q0=qSketchRegion(id+"F4",true);
            extrude(context, id + "F5", {"entities" : qUnion([Q0]), "operationType" : NewBodyOperationType.ADD, "depth" : 1.27 * mm, "offsetDistance" : 25.4 * mm});
        }
    });
